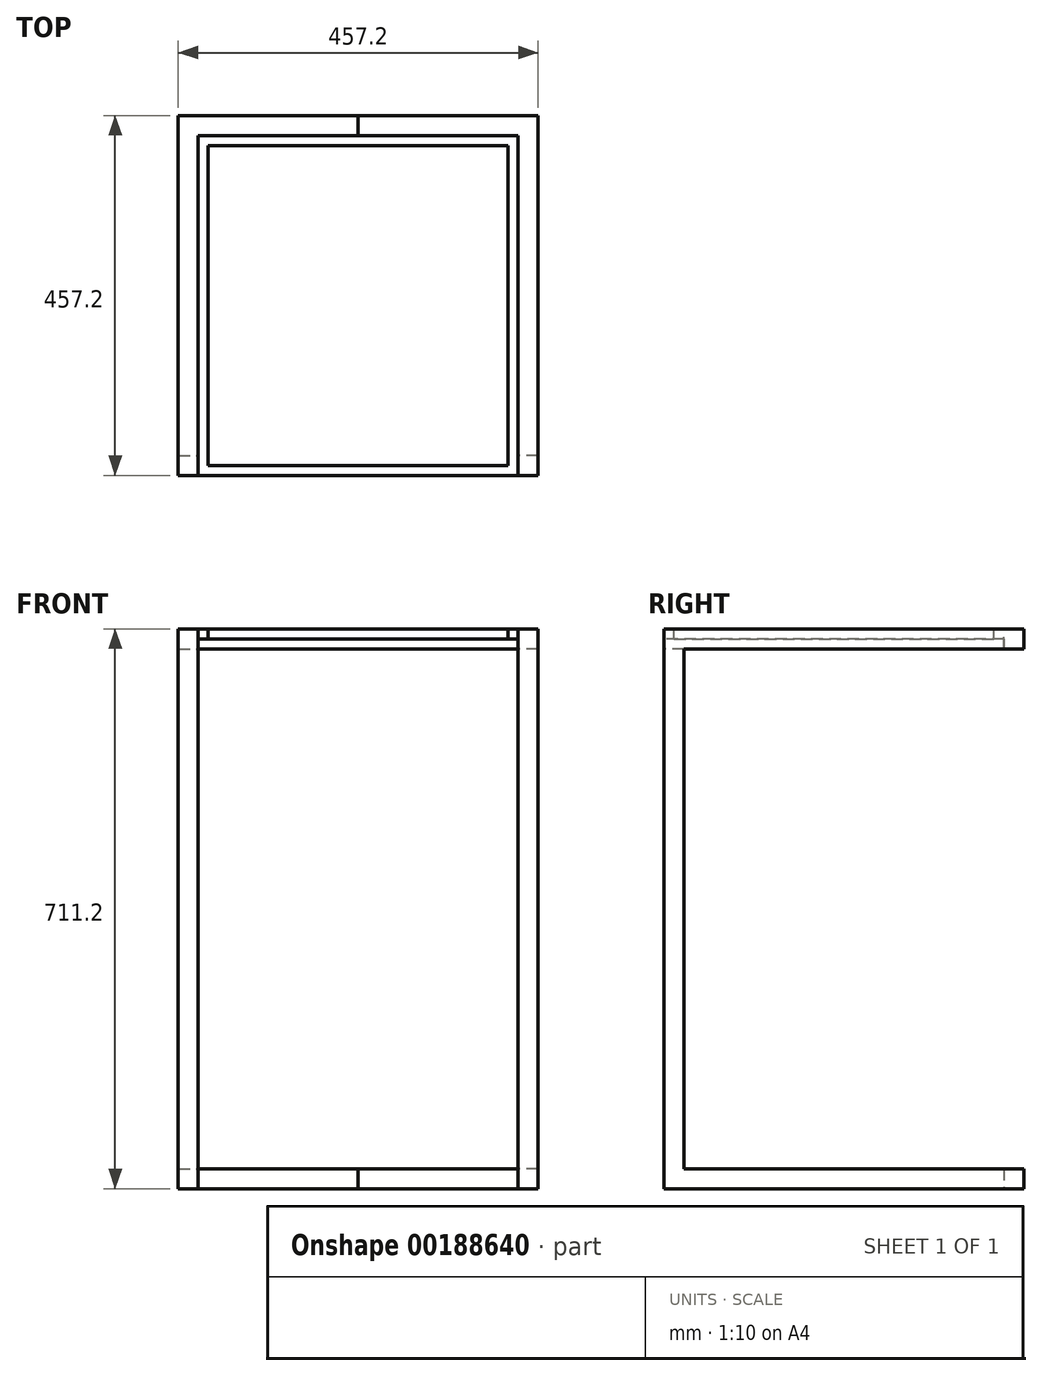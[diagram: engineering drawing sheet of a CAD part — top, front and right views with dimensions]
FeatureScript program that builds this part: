
annotation { "Feature Type Name" : "Feature", "Feature Type Description" : "" }
export const myFeature = defineFeature(function(context is Context, id is Id, definition is map)
    precondition{}
    {
        {
            var Q0;
            Q0=qCreatedBy(makeId("Top.planeOp"),FACE);
            var sketch = newSketch(context, id + "F0", { "sketchPlane" : qUnion([Q0])});
            skLineSegment(sketch, "E0.bottom", {"start": v(0, 0) * mm, "end": v(228.6, 0) * mm});
            skLineSegment(sketch, "E0.top", {"start": v(0, -25.4) * mm, "end": v(203.2, -25.4) * mm});
            skLineSegment(sketch, "E0.left", {"start": v(0, 0) * mm, "end": v(0, -25.4) * mm});
            skLineSegment(sketch, "E0.right", {"start": v(228.6, 0) * mm, "end": v(228.6, -25.4) * mm});
            skLineSegment(sketch, "E1.top", {"start": v(228.6, -457.2) * mm, "end": v(203.2, -457.2) * mm});
            skLineSegment(sketch, "E1.left", {"start": v(228.6, -25.4) * mm, "end": v(228.6, -457.2) * mm});
            skLineSegment(sketch, "E1.right", {"start": v(203.2, -25.4) * mm, "end": v(203.2, -457.2) * mm});
            skSolve(sketch);
        }
        {
            var Q0;
            Q0=makeQuery(id+"F0.imprint","IMPRINT",FACE,{"disambiguationData":[TD([[makeQuery(id+"F0.imprint","IMPRINT",EDGE,{"derivedFrom":sQuery(id+"F0.wireOp",EDGE,"E0.bottom")}),-1.0]])]});
            extrude(context, id + "F1", {"entities" : qUnion([Q0]), "depth" : 25.4 * mm});
        }
        {
            var Q0;
            Q0=qCreatedBy(makeId("Top.planeOp"),FACE);
            cPlane(context, id + "F2", {"entities" : qUnion([Q0]), "cplaneType" : CPlaneType.OFFSET, "offset" : 355.6 * mm, "width" : 152.4 * mm, "height" : 152.4 * mm});
        }
        {
            var Q0;
            Q0=makeQuery(id+"F1.opExtrude","SWEPT_BODY",BODY,{"disambiguationData":[OSD([sQuery(id+"F0.wireOp",EDGE,"E0.bottom"),sQuery(id+"F0.wireOp",EDGE,"E0.top"),sQuery(id+"F0.wireOp",EDGE,"E0.left"),sQuery(id+"F0.wireOp",EDGE,"E0.right"),sQuery(id+"F0.wireOp",EDGE,"E1.top"),sQuery(id+"F0.wireOp",EDGE,"E1.left"),sQuery(id+"F0.wireOp",EDGE,"E1.right")])]});
            var Q1;
            Q1=qCreatedBy(id+"F2.planeOp",FACE);
            mirror(context, id + "F3", {"entities" : qUnion([Q0]), "mirrorPlane" : qUnion([Q1])});
        }
        {
            var Q0;
            Q0=makeQuery(id+"F1.opExtrude","CAP_FACE",FACE,{"disambiguationData":[OSD([sQuery(id+"F0.wireOp",EDGE,"E0.bottom"),sQuery(id+"F0.wireOp",EDGE,"E0.top"),sQuery(id+"F0.wireOp",EDGE,"E0.left"),sQuery(id+"F0.wireOp",EDGE,"E0.right"),sQuery(id+"F0.wireOp",EDGE,"E1.top"),sQuery(id+"F0.wireOp",EDGE,"E1.left"),sQuery(id+"F0.wireOp",EDGE,"E1.right")])],"isStart":false});
            var sketch = newSketch(context, id + "F4", { "sketchPlane" : qUnion([Q0])});
            skLineSegment(sketch, "E2.bottom", {"start": v(228.6, -431.8) * mm, "end": v(203.2, -431.8) * mm});
            skLineSegment(sketch, "E2.top", {"start": v(228.6, -457.2) * mm, "end": v(203.2, -457.2) * mm});
            skLineSegment(sketch, "E2.left", {"start": v(228.6, -431.8) * mm, "end": v(228.6, -457.2) * mm});
            skLineSegment(sketch, "E2.right", {"start": v(203.2, -431.8) * mm, "end": v(203.2, -457.2) * mm});
            skSolve(sketch);
        }
        {
            var Q0;
            Q0=makeQuery(id+"F4.imprint","IMPRINT",FACE,{"disambiguationData":[TD([[makeQuery(id+"F4.imprint","IMPRINT",EDGE,{"derivedFrom":sQuery(id+"F4.wireOp",EDGE,"E2.bottom")}),1.0]])]});
            extrude(context, id + "F5", {"entities" : qUnion([Q0]), "operationType" : NewBodyOperationType.ADD, "depth" : 660.4 * mm});
        }
        {
            var Q0;
            Q0=makeQuery(id+"F3.opPattern","COPY",BODY,{"derivedFrom":makeQuery(id+"F1.opExtrude","SWEPT_BODY",BODY,{"disambiguationData":[OSD([sQuery(id+"F0.wireOp",EDGE,"E0.bottom"),sQuery(id+"F0.wireOp",EDGE,"E0.top"),sQuery(id+"F0.wireOp",EDGE,"E0.left"),sQuery(id+"F0.wireOp",EDGE,"E0.right"),sQuery(id+"F0.wireOp",EDGE,"E1.top"),sQuery(id+"F0.wireOp",EDGE,"E1.left"),sQuery(id+"F0.wireOp",EDGE,"E1.right")])]}),"instanceName":"1"});
            var Q1;
            Q1=makeQuery(id+"F1.opExtrude","SWEPT_BODY",BODY,{"disambiguationData":[OSD([sQuery(id+"F0.wireOp",EDGE,"E0.bottom"),sQuery(id+"F0.wireOp",EDGE,"E0.top"),sQuery(id+"F0.wireOp",EDGE,"E0.left"),sQuery(id+"F0.wireOp",EDGE,"E0.right"),sQuery(id+"F0.wireOp",EDGE,"E1.top"),sQuery(id+"F0.wireOp",EDGE,"E1.left"),sQuery(id+"F0.wireOp",EDGE,"E1.right")])]});
            var Q2;
            Q2=qCreatedBy(makeId("Right.planeOp"),FACE);
            mirror(context, id + "F6", {"entities" : qUnion([Q0, Q1]), "mirrorPlane" : qUnion([Q2])});
        }
        {
            var Q0;
            Q0=qCreatedBy(makeId("Top.planeOp"),FACE);
            cPlane(context, id + "F7", {"entities" : qUnion([Q0]), "cplaneType" : CPlaneType.OFFSET, "offset" : 685.8 * mm, "width" : 152.4 * mm, "height" : 152.4 * mm});
        }
        {
            var Q0;
            Q0=qCreatedBy(id+"F7.planeOp",FACE);
            var sketch = newSketch(context, id + "F8", { "sketchPlane" : qUnion([Q0])});
            skLineSegment(sketch, "E3.bottom", {"start": v(203.2, -25.4) * mm, "end": v(-203.2, -25.4) * mm});
            skLineSegment(sketch, "E3.top", {"start": v(203.2, -457.2) * mm, "end": v(-203.2, -457.2) * mm});
            skLineSegment(sketch, "E3.left", {"start": v(203.2, -25.4) * mm, "end": v(203.2, -457.2) * mm});
            skLineSegment(sketch, "E3.right", {"start": v(-203.2, -25.4) * mm, "end": v(-203.2, -457.2) * mm});
            skSolve(sketch);
        }
        {
            var Q0;
            Q0=makeQuery(id+"F8.imprint","IMPRINT",FACE,{"disambiguationData":[TD([[makeQuery(id+"F8.imprint","IMPRINT",EDGE,{"derivedFrom":sQuery(id+"F8.wireOp",EDGE,"E3.bottom")}),1.0]])]});
            extrude(context, id + "F9", {"entities" : qUnion([Q0]), "depth" : 25.4 * mm});
        }
        {
            var Q0;
            Q0=makeQuery(id+"F9.opExtrude","CAP_FACE",FACE,{"disambiguationData":[OSD([sQuery(id+"F8.wireOp",EDGE,"E3.bottom"),sQuery(id+"F8.wireOp",EDGE,"E3.top"),sQuery(id+"F8.wireOp",EDGE,"E3.left"),sQuery(id+"F8.wireOp",EDGE,"E3.right")])],"isStart":false});
            var sketch = newSketch(context, id + "F10", { "sketchPlane" : qUnion([Q0])});
            skLineSegment(sketch, "E4", {"start": v(-190.5, -444.5) * mm, "end": v(-190.5, -38.1) * mm});
            skLineSegment(sketch, "E5", {"start": v(-190.5, -38.1) * mm, "end": v(190.5, -38.1) * mm});
            skLineSegment(sketch, "E6", {"start": v(190.5, -38.1) * mm, "end": v(190.5, -444.5) * mm});
            skLineSegment(sketch, "E7", {"start": v(190.5, -444.5) * mm, "end": v(-190.5, -444.5) * mm});
            skSolve(sketch);
        }
        {
            var Q0;
            Q0=makeQuery(id+"F9.opExtrude","SWEPT_FACE",FACE,{"disambiguationData":[OSD([sQuery(id+"F8.wireOp",EDGE,"E3.top")])]});
            cPlane(context, id + "F11", {"entities" : qUnion([Q0]), "cplaneType" : CPlaneType.OFFSET, "offset" : 12.7 * mm, "oppositeDirection" : true, "width" : 152.4 * mm, "height" : 152.4 * mm});
        }
        {
            var Q0;
            Q0=qCreatedBy(id+"F11.planeOp",FACE);
            var sketch = newSketch(context, id + "F12", { "sketchPlane" : qUnion([Q0])});
            skLineSegment(sketch, "E8.bottom", {"start": v(-203.2, 711.2) * mm, "end": v(-190.5, 711.2) * mm});
            skLineSegment(sketch, "E8.top", {"start": v(-203.2, 698.5) * mm, "end": v(-190.5, 698.5) * mm});
            skLineSegment(sketch, "E8.left", {"start": v(-203.2, 711.2) * mm, "end": v(-203.2, 698.5) * mm});
            skLineSegment(sketch, "E8.right", {"start": v(-190.5, 711.2) * mm, "end": v(-190.5, 698.5) * mm});
            skSolve(sketch);
        }
        {
            var Q0;
            Q0 = qSketchRegion(id + "F12", true);
            var Q1;
            Q1 = qBodyType(qCreatedBy(id + "F10" ,EDGE), BodyType.WIRE);
            sweep(context, id + "F13", {"operationType" : NewBodyOperationType.REMOVE, "profiles" : qUnion([Q0]), "path" : qUnion([Q1])});
        }
    });
